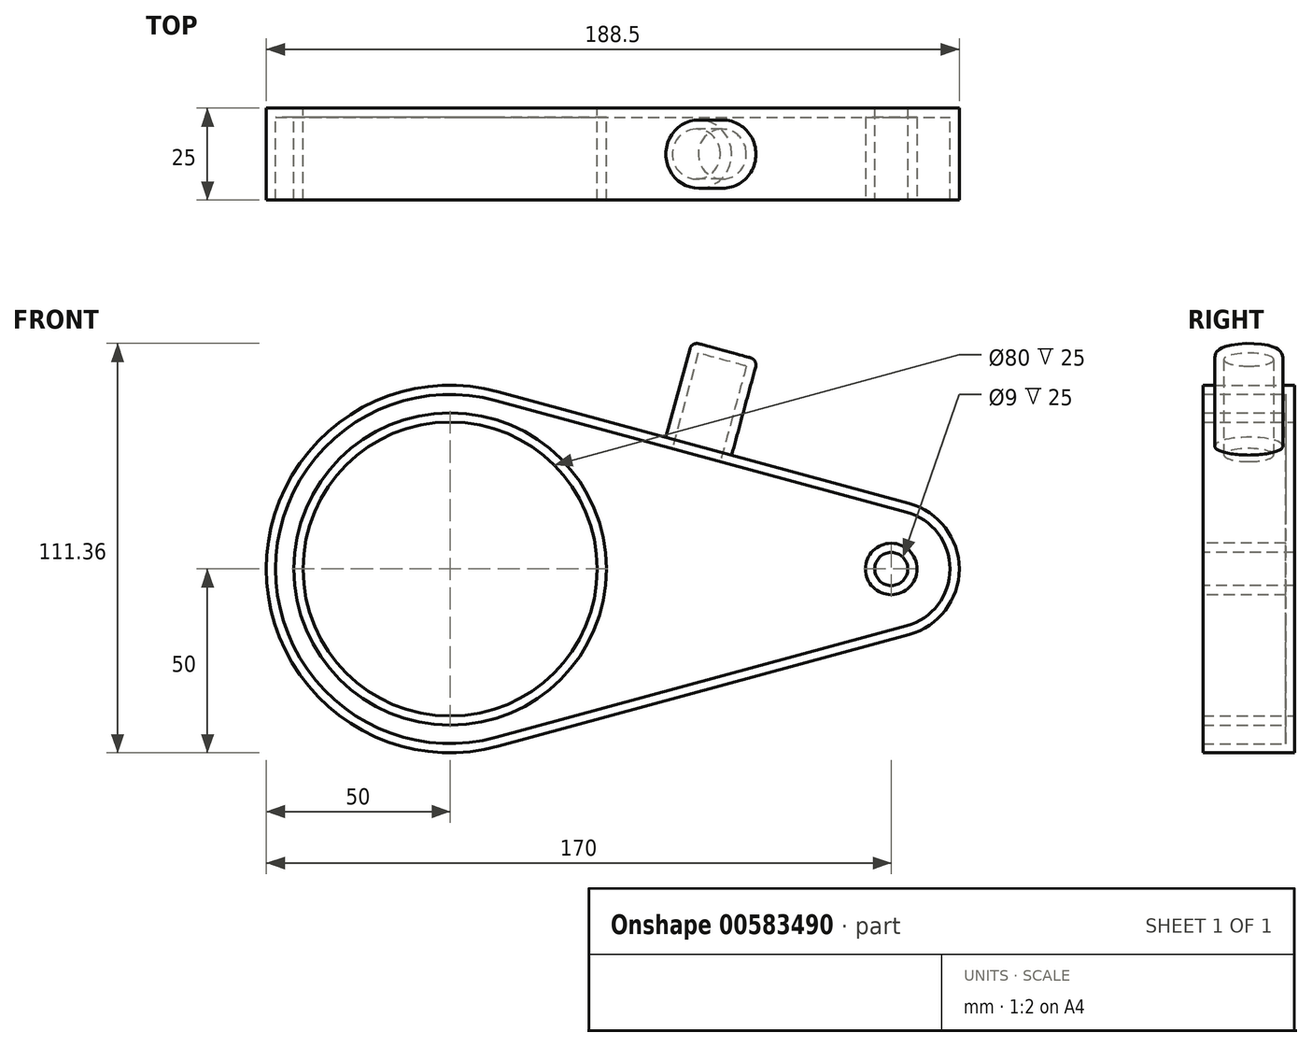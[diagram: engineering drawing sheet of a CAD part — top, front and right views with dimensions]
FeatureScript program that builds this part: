
annotation { "Feature Type Name" : "Feature", "Feature Type Description" : "" }
export const myFeature = defineFeature(function(context is Context, id is Id, definition is map)
    precondition{}
    {
        {
            var Q0;
            Q0=qCreatedBy(makeId("Front.planeOp"),FACE);
            var sketch = newSketch(context, id + "F0", { "sketchPlane" : qUnion([Q0])});
            skCircle(sketch, "E0", {"center": v(0, 0) * mm, "radius": 50 * mm});
            skCircle(sketch, "E1", {"center": v(120, 0) * mm, "radius": 18.5 * mm});
            skLineSegment(sketch, "E2", {"start": v(13.13, 48.25) * mm, "end": v(124.86, 17.85) * mm});
            skLineSegment(sketch, "E3", {"start": v(13.13, -48.25) * mm, "end": v(124.86, -17.85) * mm});
            skCircle(sketch, "E4", {"center": v(0, 0) * mm, "radius": 40 * mm});
            skSolve(sketch);
        }
        {
            var Q0;
            Q0=qSketchRegion(id+"F0",true);
            extrude(context, id + "F1", {"entities" : qUnion([Q0]), "depth" : 25 * mm, "offsetDistance" : 25 * mm});
        }
        {
            var Q0;
            Q0=makeQuery(id+"F1.opExtrude","SWEPT_FACE",FACE,{"disambiguationData":[OSD([sQuery(id+"F0.wireOp",EDGE,"E2")])]});
            var sketch = newSketch(context, id + "F2", { "sketchPlane" : qUnion([Q0])});
            skCircle(sketch, "E5", {"center": v(56.48, -12.5) * mm, "radius": 9.28 * mm});
            skPoint(sketch, "E5.centerSnap0", {"position": v(0, -12.5) * mm});
            skSolve(sketch);
        }
        {
            var Q0;
            Q0=qSketchRegion(id+"F2",true);
            extrude(context, id + "F3", {"entities" : qUnion([Q0]), "operationType" : NewBodyOperationType.ADD, "depth" : 26.9 * mm, "offsetDistance" : 25 * mm});
        }
        {
            var Q0;
            Q0=makeQuery(id+"F3.opExtrude","CAP_FACE",FACE,{"disambiguationData":[OSD([sQuery(id+"F2.wireOp",EDGE,"E5")])],"isStart":false});
            var Q1;
            Q1=makeQuery(id+"F3.opExtrude","CAP_EDGE",EDGE,{"disambiguationData":[OSD([sQuery(id+"F2.wireOp",EDGE,"E5")])],"isStart":true});
            fillet(context, id + "F4", {"entities" : qUnion([Q0, Q1]), "radius" : 2 * mm, "tangentPropagation" : true, "allowEdgeOverflow" : false});
        }
        {
            var Q0;
            Q0=makeQuery(id+"F1.opExtrude","CAP_FACE",FACE,{"disambiguationData":[OSD([sQuery(id+"F0.wireOp",EDGE,"E0"),sQuery(id+"F0.wireOp",EDGE,"E1"),sQuery(id+"F0.wireOp",EDGE,"E2"),sQuery(id+"F0.wireOp",EDGE,"E3"),sQuery(id+"F0.wireOp",EDGE,"E4")])],"isStart":false});
            var sketch = newSketch(context, id + "F5", { "sketchPlane" : qUnion([Q0])});
            skCircle(sketch, "E6", {"center": v(120, 0) * mm, "radius": 4.5 * mm});
            skSolve(sketch);
        }
        {
            var Q0;
            Q0=makeQuery(id+"F5.imprint","IMPRINT",FACE,{"disambiguationData":[TD([[makeQuery(id+"F5.imprint","IMPRINT",EDGE,{"derivedFrom":sQuery(id+"F5.wireOp",EDGE,"E6")}),1.0]])]});
            extrude(context, id + "F6", {"entities" : qUnion([Q0]), "operationType" : NewBodyOperationType.REMOVE, "endBound" : BoundingType.THROUGH_ALL, "oppositeDirection" : true, "depth" : 25 * mm, "offsetDistance" : 25 * mm});
        }
        {
            var Q0;
            Q0=makeQuery(id+"F1.opExtrude","CAP_FACE",FACE,{"disambiguationData":[OSD([sQuery(id+"F0.wireOp",EDGE,"E0"),sQuery(id+"F0.wireOp",EDGE,"E1"),sQuery(id+"F0.wireOp",EDGE,"E2"),sQuery(id+"F0.wireOp",EDGE,"E3"),sQuery(id+"F0.wireOp",EDGE,"E4")])],"isStart":false});
            shell(context, id + "F7", {"entities" : qUnion([Q0]), "thickness" : 2.5 * mm});
        }
    });
